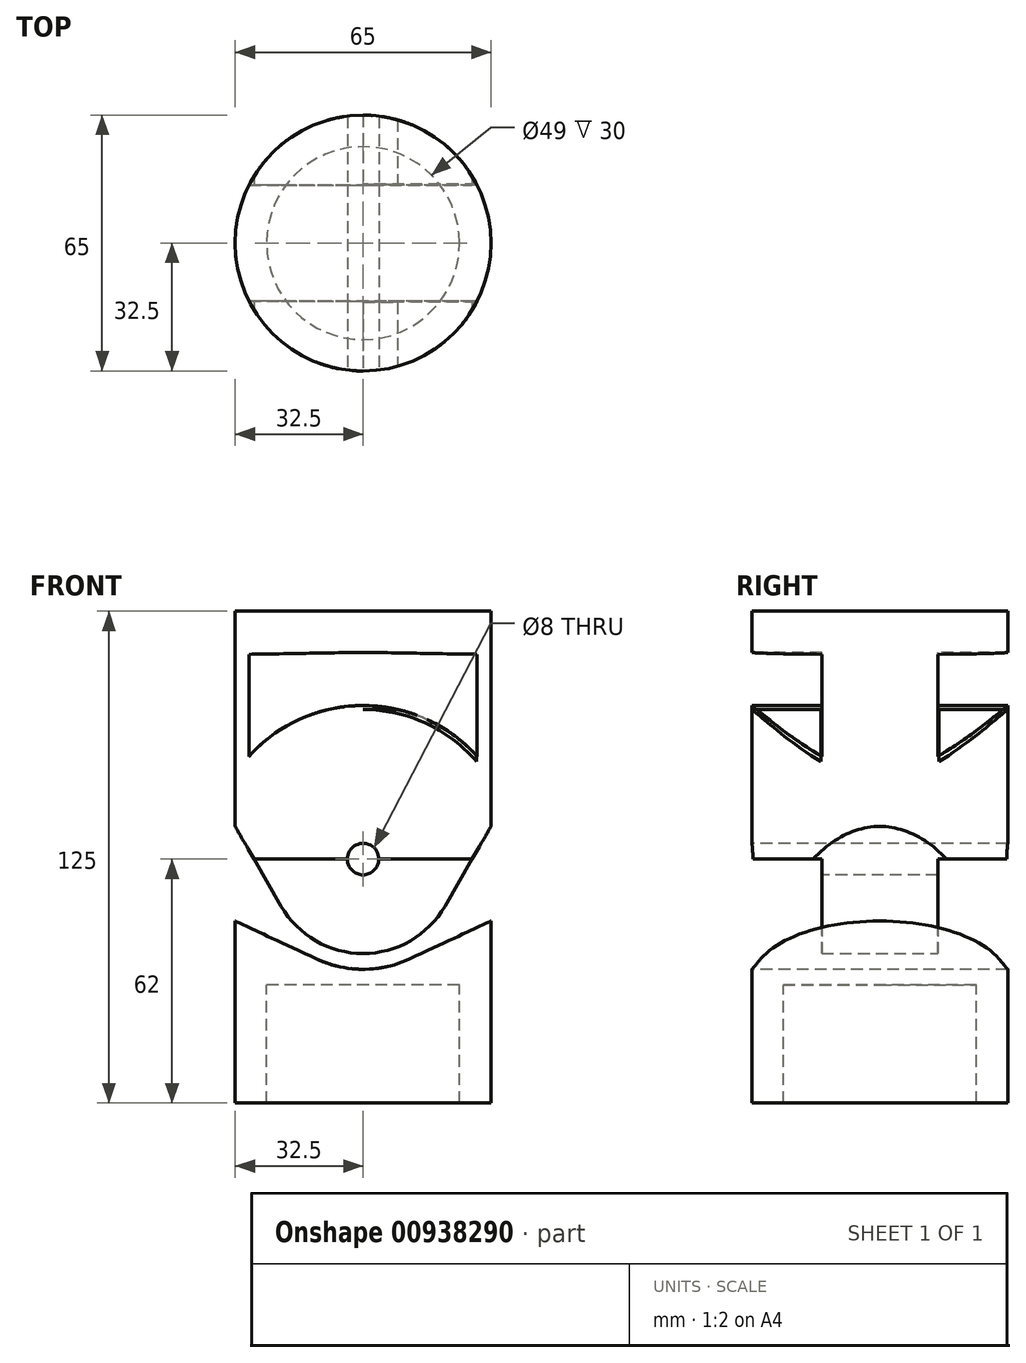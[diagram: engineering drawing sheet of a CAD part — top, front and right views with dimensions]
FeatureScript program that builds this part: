
annotation { "Feature Type Name" : "Feature", "Feature Type Description" : "" }
export const myFeature = defineFeature(function(context is Context, id is Id, definition is map)
    precondition{}
    {
        {
            var Q0;
            Q0=qCreatedBy(makeId("Front.planeOp"),FACE);
            var sketch = newSketch(context, id + "F0", { "sketchPlane" : qUnion([Q0])});
            skLineSegment(sketch, "E0", {"start": v(0, 0) * mm, "end": v(0, -84.6) * mm, "construction": true});
            skLineSegment(sketch, "E1", {"start": v(0, 0) * mm, "end": v(33, 0) * mm, "construction": true});
            skLineSegment(sketch, "E2", {"start": v(33, 0) * mm, "end": v(33, -84.6) * mm, "construction": true});
            skLineSegment(sketch, "E3", {"start": v(33, -84.6) * mm, "end": v(38, -84.6) * mm, "construction": true});
            skLineSegment(sketch, "E4", {"start": v(38, -84.6) * mm, "end": v(38, 0) * mm, "construction": true});
            skLineSegment(sketch, "E5", {"start": v(38, 0) * mm, "end": v(33, 0) * mm, "construction": true});
            skArc(sketch, "E6", {"start": v(0, 0) * mm, "mid": v(26.87, -11.13) * mm, "end": v(38, -38) * mm, "construction": true});
            skArc(sketch, "E7", {"start": v(0, -63) * mm, "mid": v(12.5, -59.65) * mm, "end": v(21.65, -50.5) * mm, "construction": true});
            skLineSegment(sketch, "E8", {"start": v(21.65, -50.5) * mm, "end": v(59.2, 14.52) * mm, "construction": true});
            skLineSegment(sketch, "E9", {"start": v(10.57, -60.66) * mm, "end": v(33, -50.2) * mm, "construction": true});
            skLineSegment(sketch, "E10", {"start": v(0, -38) * mm, "end": v(21.65, -50.5) * mm, "construction": true});
            skLineSegment(sketch, "E11", {"start": v(33, -50.2) * mm, "end": v(38, -50.2) * mm, "construction": true});
            skSolve(sketch);
        }
        {
            var Q0;
            Q0=qCreatedBy(makeId("Top.planeOp"),FACE);
            var sketch = newSketch(context, id + "F1", { "sketchPlane" : qUnion([Q0])});
            skPoint(sketch, "E12.0", {"position": v(33, 0) * mm});
            skPoint(sketch, "E12.1", {"position": v(38, 0) * mm});
            skCircle(sketch, "E13", {"center": v(0, 0) * mm, "radius": 33 * mm});
            skCircle(sketch, "E14", {"center": v(0, 0) * mm, "radius": 38 * mm});
            skCircle(sketch, "E15", {"center": v(0, 0) * mm, "radius": 32.5 * mm});
            skCircle(sketch, "E16", {"center": v(0, 0) * mm, "radius": 24.5 * mm});
            skCircle(sketch, "E17", {"center": v(0, 0) * mm, "radius": 118.1 * mm});
            skSolve(sketch);
        }
        {
            var Q0;
            Q0=qCreatedBy(makeId("Front.planeOp"),FACE);
            var sketch = newSketch(context, id + "F2", { "sketchPlane" : qUnion([Q0])});
            skPoint(sketch, "E18.0", {"position": v(33, -50.2) * mm});
            skPoint(sketch, "E18.1", {"position": v(38, -50.2) * mm});
            skPoint(sketch, "E19.0", {"position": v(0, -38) * mm});
            skArc(sketch, "E20.0", {"start": v(0, 0) * mm, "mid": v(26.87, -11.13) * mm, "end": v(38, -38) * mm});
            skLineSegment(sketch, "E21", {"start": v(0, 0) * mm, "end": v(38, 0) * mm});
            skLineSegment(sketch, "E22", {"start": v(38, 0) * mm, "end": v(38, -38) * mm});
            skLineSegment(sketch, "E23", {"start": v(0, 0) * mm, "end": v(0, -50.2) * mm, "construction": true});
            skCircle(sketch, "E24", {"center": v(0, -38) * mm, "radius": 4.1 * mm});
            skArc(sketch, "E25.MirrorCS", {"start": v(0, 0) * mm, "mid": v(-26.87, -11.13) * mm, "end": v(-38, -38) * mm});
            skLineSegment(sketch, "E26.MirrorCS", {"start": v(0, 0) * mm, "end": v(-38, 0) * mm});
            skLineSegment(sketch, "E27.MirrorCS", {"start": v(-38, 0) * mm, "end": v(-38, -38) * mm});
            skArc(sketch, "E28.0", {"start": v(0, -63) * mm, "mid": v(5.41, -62.4) * mm, "end": v(10.57, -60.66) * mm, "construction": true});
            skLineSegment(sketch, "E28.1", {"start": v(10.57, -60.66) * mm, "end": v(33, -50.2) * mm, "construction": true});
            skLineSegment(sketch, "E28.2", {"start": v(33, -50.2) * mm, "end": v(38, -50.2) * mm, "construction": true});
            skPoint(sketch, "E29.orphan", {"position": v(21.65, -50.5) * mm});
            skLineSegment(sketch, "E30.0", {"start": v(33.67, -53.2) * mm, "end": v(38, -53.2) * mm});
            skLineSegment(sketch, "E30.1", {"start": v(11.83, -63.38) * mm, "end": v(33.67, -53.2) * mm});
            skArc(sketch, "E30.2", {"start": v(0, -66) * mm, "mid": v(6.06, -65.34) * mm, "end": v(11.83, -63.38) * mm});
            skArc(sketch, "E31.MirrorCS", {"start": v(0, -66) * mm, "mid": v(-6.06, -65.34) * mm, "end": v(-11.83, -63.38) * mm});
            skLineSegment(sketch, "E32.MirrorCS", {"start": v(-33.67, -53.2) * mm, "end": v(-38, -53.2) * mm});
            skLineSegment(sketch, "E33.MirrorCS", {"start": v(-11.83, -63.38) * mm, "end": v(-33.67, -53.2) * mm});
            skLineSegment(sketch, "E34", {"start": v(-38, -38) * mm, "end": v(-38, -53.2) * mm});
            skLineSegment(sketch, "E35", {"start": v(38, -38) * mm, "end": v(38, -53.2) * mm});
            skSolve(sketch);
        }
        {
            var Q0;
            Q0=makeQuery(id+"F1.imprint","IMPRINT",FACE,{"disambiguationData":[TD([[makeQuery(id+"F1.imprint","IMPRINT",EDGE,{"derivedFrom":sQuery(id+"F1.wireOp",EDGE,"E13")}),-1.0]])]});
            extrude(context, id + "F3", {"entities" : qUnion([Q0]), "oppositeDirection" : true, "depth" : 100 * mm, "offsetDistance" : 25 * mm});
        }
        {
            var Q0;
            Q0=makeQuery(id+"F1.imprint","IMPRINT",FACE,{"disambiguationData":[TD([[makeQuery(id+"F1.imprint","IMPRINT",EDGE,{"derivedFrom":sQuery(id+"F1.wireOp",EDGE,"E15")}),1.0]])]});
            extrude(context, id + "F4", {"entities" : qUnion([Q0]), "oppositeDirection" : true, "depth" : 100 * mm, "offsetDistance" : 25 * mm});
        }
        {
            var Q0;
            Q0=makeQuery(id+"F1.imprint","IMPRINT",FACE,{"disambiguationData":[TD([[makeQuery(id+"F1.imprint","IMPRINT",EDGE,{"derivedFrom":sQuery(id+"F1.wireOp",EDGE,"E16")}),1.0]])]});
            extrude(context, id + "F5", {"entities" : qUnion([Q0]), "operationType" : NewBodyOperationType.ADD, "oppositeDirection" : true, "depth" : 70 * mm, "offsetDistance" : 25 * mm});
        }
        {
            var Q0;
            Q0=makeQuery(id+"F2.imprint","IMPRINT",FACE,{"disambiguationData":[TD([[makeQuery(id+"F2.imprint","IMPRINT",EDGE,{"derivedFrom":sQuery(id+"F2.wireOp",EDGE,"E25.MirrorCS")}),-1.0]])]});
            var Q1;
            Q1=makeQuery(id+"F2.imprint","IMPRINT",FACE,{"disambiguationData":[TD([[makeQuery(id+"F2.imprint","IMPRINT",EDGE,{"derivedFrom":sQuery(id+"F2.wireOp",EDGE,"E20.0")}),1.0]])]});
            var Q2;
            Q2=makeQuery(id+"F2.imprint","IMPRINT",FACE,{"disambiguationData":[TD([[makeQuery(id+"F2.imprint","IMPRINT",EDGE,{"derivedFrom":sQuery(id+"F2.wireOp",EDGE,"E24")}),1.0]])]});
            extrude(context, id + "F6", {"entities" : qUnion([Q0, Q1, Q2]), "operationType" : NewBodyOperationType.REMOVE, "endBound" : BoundingType.SYMMETRIC, "oppositeDirection" : true, "depth" : 200 * mm, "offsetDistance" : 25 * mm});
        }
        {
            var Q0;
            Q0=makeQuery(id+"F2.imprint","IMPRINT",FACE,{"disambiguationData":[TD([[makeQuery(id+"F2.imprint","IMPRINT",EDGE,{"derivedFrom":sQuery(id+"F2.wireOp",EDGE,"E20.0")}),-1.0]])]});
            extrude(context, id + "F7", {"entities" : qUnion([Q0]), "operationType" : NewBodyOperationType.REMOVE, "endBound" : BoundingType.SYMMETRIC, "oppositeDirection" : true, "depth" : 30 * mm, "offsetDistance" : 25 * mm});
        }
        {
            var Q0;
            Q0=qCreatedBy(makeId("Front.planeOp"),FACE);
            var sketch = newSketch(context, id + "F8", { "sketchPlane" : qUnion([Q0])});
            skPoint(sketch, "E36.0", {"position": v(0, -38) * mm});
            skPoint(sketch, "E37.0", {"position": v(33, 0) * mm});
            skPoint(sketch, "E38.0", {"position": v(38, 0) * mm});
            skArc(sketch, "E39", {"start": v(0, 1) * mm, "mid": v(20.53, -4.84) * mm, "end": v(34.91, -20.62) * mm});
            skLineSegment(sketch, "E40.0", {"start": v(34.91, -23) * mm, "end": v(34.91, -53.2) * mm, "construction": true});
            skLineSegment(sketch, "E41", {"start": v(34.91, -20.62) * mm, "end": v(38, -20.62) * mm});
            skLineSegment(sketch, "E42", {"start": v(38, -20.62) * mm, "end": v(38, -38) * mm});
            skLineSegment(sketch, "E43", {"start": v(38, -38) * mm, "end": v(0, -38) * mm});
            skLineSegment(sketch, "E44", {"start": v(0, -38) * mm, "end": v(0, 0) * mm, "construction": true});
            skArc(sketch, "E45.MirrorCS", {"start": v(0, 1) * mm, "mid": v(-20.53, -4.84) * mm, "end": v(-34.91, -20.62) * mm});
            skLineSegment(sketch, "E46.MirrorCS", {"start": v(-34.91, -20.62) * mm, "end": v(-38, -20.62) * mm});
            skLineSegment(sketch, "E47.MirrorCS", {"start": v(-38, -20.62) * mm, "end": v(-38, -38) * mm});
            skLineSegment(sketch, "E48.MirrorCS", {"start": v(-38, -38) * mm, "end": v(0, -38) * mm});
            skArc(sketch, "E49.0", {"start": v(0, -63) * mm, "mid": v(12.5, -59.65) * mm, "end": v(21.65, -50.5) * mm, "construction": true});
            skLineSegment(sketch, "E49.1", {"start": v(21.65, -50.5) * mm, "end": v(59.2, 14.52) * mm, "construction": true});
            skLineSegment(sketch, "E50.0", {"start": v(20.78, -50) * mm, "end": v(57.46, 13.52) * mm});
            skArc(sketch, "E50.1", {"start": v(0, -62) * mm, "mid": v(12, -58.78) * mm, "end": v(20.78, -50) * mm});
            skLineSegment(sketch, "E51", {"start": v(57.46, 13.52) * mm, "end": v(0, 14.52) * mm});
            skArc(sketch, "E52.MirrorCS", {"start": v(0, -62) * mm, "mid": v(-12, -58.78) * mm, "end": v(-20.78, -50) * mm});
            skLineSegment(sketch, "E53.MirrorCS", {"start": v(-20.78, -50) * mm, "end": v(-57.46, 13.52) * mm});
            skLineSegment(sketch, "E54.MirrorCS", {"start": v(-57.46, 13.52) * mm, "end": v(0, 14.52) * mm});
            skCircle(sketch, "E55", {"center": v(0, -38) * mm, "radius": 4 * mm});
            skSolve(sketch);
        }
        {
            var Q0;
            Q0=makeQuery(id+"F1.imprint","IMPRINT",FACE,{"disambiguationData":[TD([[makeQuery(id+"F1.imprint","IMPRINT",EDGE,{"derivedFrom":sQuery(id+"F1.wireOp",EDGE,"E13")}),-1.0]])]});
            var Q1;
            Q1=sQuery(id+"F8.wireOp",VERTEX,"E36.0");
            extrude(context, id + "F9", {"entities" : qUnion([Q0]), "endBound" : BoundingType.UP_TO_VERTEX, "oppositeDirection" : true, "depth" : 25 * mm, "endBoundEntityVertex" : qUnion([Q1]), "offsetDistance" : 25 * mm, "hasSecondDirection" : true, "secondDirectionOppositeDirection" : false, "secondDirectionDepth" : 25 * mm});
        }
        {
            var Q0;
            Q0=makeQuery(id+"F1.imprint","IMPRINT",FACE,{"disambiguationData":[TD([[makeQuery(id+"F1.imprint","IMPRINT",EDGE,{"derivedFrom":sQuery(id+"F1.wireOp",EDGE,"E15")}),1.0]])]});
            var Q1;
            Q1=makeQuery(id+"F1.imprint","IMPRINT",FACE,{"disambiguationData":[TD([[makeQuery(id+"F1.imprint","IMPRINT",EDGE,{"derivedFrom":sQuery(id+"F1.wireOp",EDGE,"E16")}),1.0]])]});
            var Q2;
            Q2=sQuery(id+"F8.wireOp",VERTEX,"E36.0");
            extrude(context, id + "F10", {"entities" : qUnion([Q0, Q1]), "endBound" : BoundingType.UP_TO_VERTEX, "oppositeDirection" : true, "depth" : 25 * mm, "endBoundEntityVertex" : qUnion([Q2]), "offsetDistance" : 25 * mm, "hasSecondDirection" : true, "secondDirectionOppositeDirection" : false, "secondDirectionDepth" : 25 * mm});
        }
        {
            var Q0;
            Q0=makeQuery(id+"F8.imprint","IMPRINT",FACE,{"disambiguationData":[TD([[makeQuery(id+"F8.imprint","IMPRINT",EDGE,{"derivedFrom":sQuery(id+"F8.wireOp",EDGE,"E39")}),-1.0]])]});
            var Q1;
            {var subQ0=sQuery(id+"F8.wireOp",EDGE,"E47.MirrorCS");Q1=makeQuery(id+"F8.imprint","IMPRINT",FACE,{"disambiguationData":[TD([[makeQuery(id+"F8.imprint","IMPRINT",EDGE,{"derivedFrom":subQ0}),1.0]])]});}
            var Q2;
            {var subQ0=sQuery(id+"F8.wireOp",EDGE,"E42");Q2=makeQuery(id+"F8.imprint","IMPRINT",FACE,{"disambiguationData":[TD([[makeQuery(id+"F8.imprint","IMPRINT",EDGE,{"derivedFrom":subQ0}),-1.0]])]});}
            var Q3;
            {var subQ0=sQuery(id+"F8.wireOp",EDGE,"E48.MirrorCS");var subQ1=sQuery(id+"F8.wireOp",EDGE,"E43");var subQ2=makeQuery(id+"F8.imprint","INTERSECT",VERTEX,{"derivedFrom":[subQ1,subQ0]});Q3=makeQuery(id+"F8.imprint","IMPRINT",FACE,{"disambiguationData":[TD([[makeQuery(id+"F8.imprint","IMPRINT",EDGE,{"disambiguationData":[TD([[subQ2,1.0]])],"derivedFrom":subQ1}),-1.0]])]});}
            var Q4;
            {var subQ0=sQuery(id+"F8.wireOp",EDGE,"E48.MirrorCS");var subQ1=sQuery(id+"F8.wireOp",EDGE,"E43");var subQ2=makeQuery(id+"F8.imprint","INTERSECT",VERTEX,{"derivedFrom":[subQ1,subQ0]});Q4=makeQuery(id+"F8.imprint","IMPRINT",FACE,{"disambiguationData":[TD([[makeQuery(id+"F8.imprint","IMPRINT",EDGE,{"disambiguationData":[TD([[subQ2,1.0]])],"derivedFrom":subQ1}),1.0]])]});}
            var Q5;
            {var subQ0=sQuery(id+"F8.wireOp",EDGE,"E50.1");Q5=makeQuery(id+"F8.imprint","IMPRINT",FACE,{"disambiguationData":[TD([[makeQuery(id+"F8.imprint","IMPRINT",EDGE,{"derivedFrom":subQ0}),1.0]])]});}
            extrude(context, id + "F11", {"entities" : qUnion([Q0, Q1, Q2, Q3, Q4, Q5]), "operationType" : NewBodyOperationType.REMOVE, "endBound" : BoundingType.SYMMETRIC, "oppositeDirection" : true, "depth" : 200 * mm, "offsetDistance" : 25 * mm});
        }
        {
            var Q0;
            {var subQ6=sQuery(id+"F8.wireOp",EDGE,"E39");Q0=makeQuery(id+"F8.imprint","IMPRINT",FACE,{"disambiguationData":[TD([[makeQuery(id+"F8.imprint","IMPRINT",EDGE,{"derivedFrom":subQ6}),1.0]])]});}
            var Q1;
            {var subQ0=sQuery(id+"F8.wireOp",EDGE,"E50.1");Q1=makeQuery(id+"F8.imprint","IMPRINT",FACE,{"disambiguationData":[TD([[makeQuery(id+"F8.imprint","IMPRINT",EDGE,{"derivedFrom":subQ0}),1.0]])]});}
            var Q2;
            {var subQ2=sQuery(id+"F8.wireOp",EDGE,"E39");Q2=makeQuery(id+"F8.imprint","IMPRINT",FACE,{"disambiguationData":[TD([[makeQuery(id+"F8.imprint","IMPRINT",EDGE,{"derivedFrom":subQ2}),-1.0]])]});}
            extrude(context, id + "F12", {"entities" : qUnion([Q0, Q1, Q2]), "operationType" : NewBodyOperationType.ADD, "endBound" : BoundingType.SYMMETRIC, "depth" : 29.5 * mm, "offsetDistance" : 25 * mm});
        }
        {
            var Q0;
            Q0=makeQuery(id+"F1.imprint","IMPRINT",FACE,{"disambiguationData":[TD([[makeQuery(id+"F1.imprint","IMPRINT",EDGE,{"derivedFrom":sQuery(id+"F1.wireOp",EDGE,"E13")}),-1.0]])]});
            var Q1;
            Q1=makeQuery(id+"F1.imprint","IMPRINT",FACE,{"disambiguationData":[TD([[makeQuery(id+"F1.imprint","IMPRINT",EDGE,{"derivedFrom":sQuery(id+"F1.wireOp",EDGE,"E13")}),1.0]])]});
            var Q2;
            Q2=makeQuery(id+"F1.imprint","IMPRINT",FACE,{"disambiguationData":[TD([[makeQuery(id+"F1.imprint","IMPRINT",EDGE,{"derivedFrom":sQuery(id+"F1.wireOp",EDGE,"E14")}),-1.0]])]});
            extrude(context, id + "F13", {"entities" : qUnion([Q0, Q1, Q2]), "operationType" : NewBodyOperationType.REMOVE, "endBound" : BoundingType.THROUGH_ALL, "oppositeDirection" : true, "depth" : 25 * mm, "offsetDistance" : 25 * mm, "hasSecondDirection" : true, "secondDirectionBound" : SecondDirectionBoundingType.THROUGH_ALL, "secondDirectionOppositeDirection" : false, "secondDirectionDepth" : 25 * mm});
        }
    });
